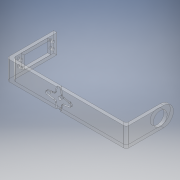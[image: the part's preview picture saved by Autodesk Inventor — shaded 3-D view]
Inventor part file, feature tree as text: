
AUTODESK INVENTOR PART (.ipt)
format: ipt  version: 2018 (Build 220112000, 112)  size: 241,664 bytes
history: native  units: mm
features: extrude x5, sketch x4, fillet x2
ambient origin geometry x8: Origin, YZ Plane, XZ Plane, XY Plane, X Axis, Y Axis, Z Axis, Center Point
bodies: Solid1 (feature_tree)
feature tree (11):
  extrude  "Outline"  Depth=68.0mm
  extrude  "Servo Mount"  Depth=73.0mm
  extrude  "Idler Mount"  Depth=73.0mm
  sketch  "Sketch4"  dims[d6=5.0mm d7=30.0mm d8=0.0mm d9=30.0mm d10=20.0mm d11=41.0mm d12=4.0mm d13=5.0mm d14=4.0mm d15=5.0mm d16=4.0mm d17=5.0mm d18=4.0mm d19=5.0mm d20=4.0mm d21=4.0mm d22=4.0mm d23=4.0mm d24=10.0mm d25=0.0mm d26=11.0mm d27=21.5mm d28=14.5mm d29=0.0mm d35=2.0mm d37=1.745329mm d39=1.745329mm d41=1.745329mm d43=1.745329mm d45=1.745329mm d47=1.745329mm d49=1.745329mm d51=1.745329mm d52=2.0mm d53=2.0mm d54=80.0mm d55=6.5mm d56=6.5mm d57=14.0mm d58=14.0mm d59=14.0mm d60=14.0mm d61=1.5mm d62=1.5mm d63=1.5mm d64=1.5mm d65=2.0mm d66=0.0mm d67=22.0mm d68=0.0mm d69=4.0mm d70=5.0mm d73=15.0mm]
  extrude  "Bottom Servo indent"  Depth=30.0mm TaperAngle=0.0deg
  extrude  "Bottom Servo Mounting Holse"  Depth=30.0mm
  fillet  "Strengthening Fillet"  Radius=20.0mm
  fillet  "Rounded Idler Post"  Radius=41.0mm
  sketch  "Sketch1"  dims[d0=175.0mm d1=68.0mm]
  sketch  "Sketch2"  dims[d2=5.0mm d3=73.0mm]
  sketch  "Sketch3"  dims[d4=185.0mm d5=73.0mm]
